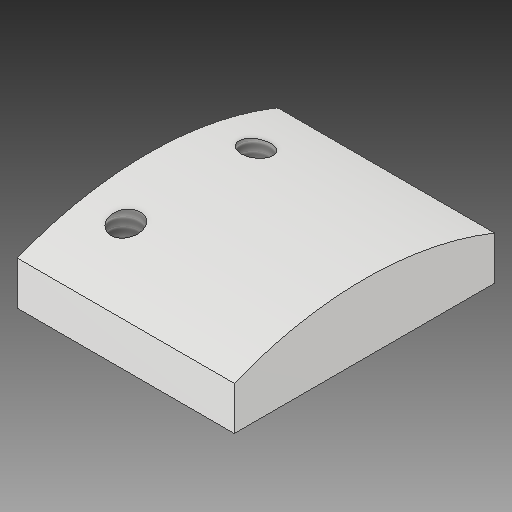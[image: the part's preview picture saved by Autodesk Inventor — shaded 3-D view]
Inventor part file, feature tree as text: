
AUTODESK INVENTOR PART (.ipt)
format: ipt  version: 2017 (Build 210142000, 142)  size: 107,008 bytes
history: native  units: in
note: dims shown in document units (in); Inventor stores cm internally (conversion verified against a paired STEP export)
features: other x3, sketch x2
ambient origin geometry x8: Origin, YZ Plane, XZ Plane, XY Plane, X Axis, Y Axis, Z Axis, Center Point
bodies: Solid1 (feature_tree)
feature tree (5):
  other  "TensionerPusher4.ipt"
  other  "Solid1::TensionerPusher4.ipt"
  other  "TaggingFeature1"
  sketch  "Sketch1"  dims[d0=0.3937in]
  sketch  "Sketch2"
